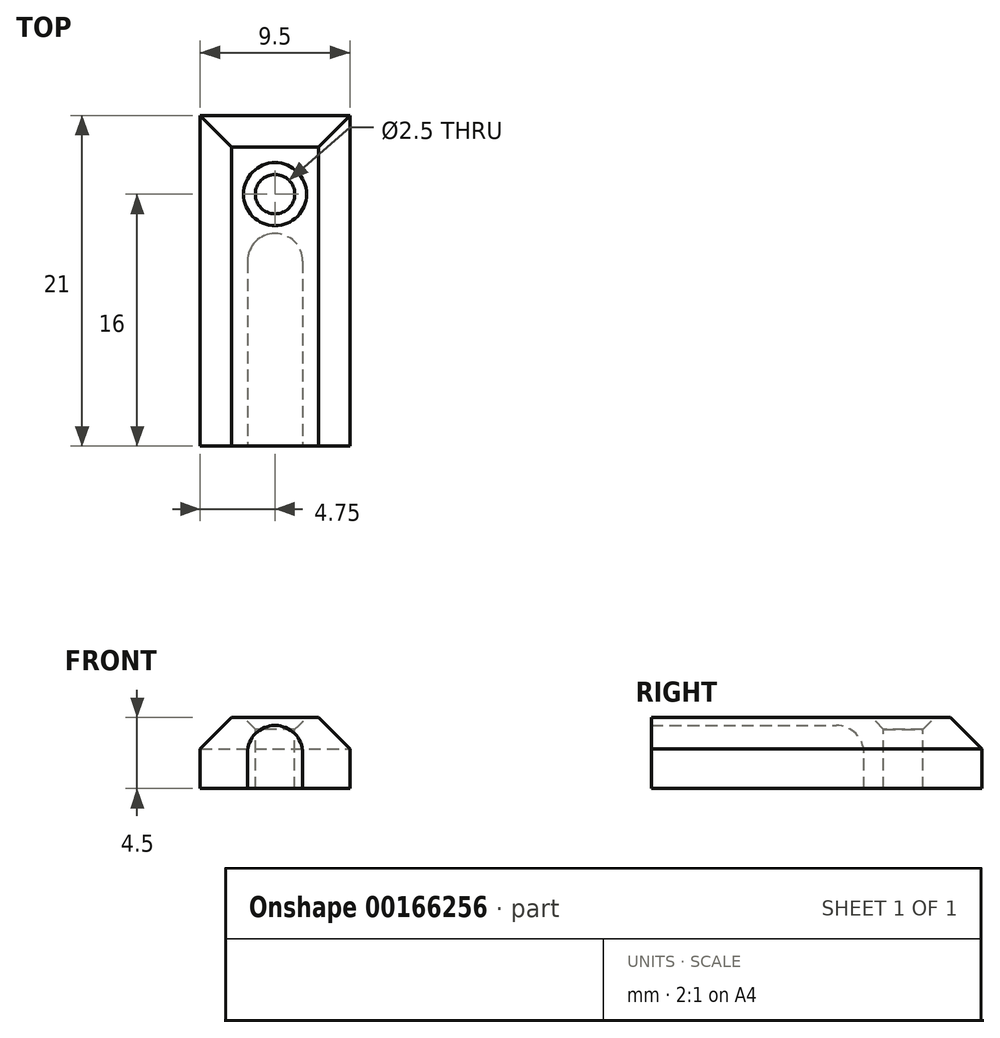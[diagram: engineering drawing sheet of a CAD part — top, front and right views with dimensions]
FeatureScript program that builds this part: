
annotation { "Feature Type Name" : "Feature", "Feature Type Description" : "" }
export const myFeature = defineFeature(function(context is Context, id is Id, definition is map)
    precondition{}
    {
        {
            assignVariable(context, id + "F0", {"name" : "Main_Length", "anyValue" : 21});
        }
        {
            assignVariable(context, id + "F1", {"name" : "Bore_Diam", "anyValue" : 3.5});
        }
        {
            assignVariable(context, id + "F2", {"name" : "Bore_Offset", "anyValue" : 0.5});
        }
        {
            assignVariable(context, id + "F3", {"name" : "Chamfer", "anyValue" : 2});
        }
        {
            assignVariable(context, id + "F4", {"name" : "Hole_Diam", "anyValue" : 2.5});
        }
        {
            var Q0;
            Q0=qCreatedBy(makeId("Front.planeOp"),FACE);
            var sketch = newSketch(context, id + "F5", { "sketchPlane" : qUnion([Q0])});
            skLineSegment(sketch, "E0.bottom", {"start": v(4.75, 4.5) * mm, "end": v(-4.75, 4.5) * mm});
            skLineSegment(sketch, "E0.left", {"start": v(4.75, 4.5) * mm, "end": v(4.75, 0) * mm});
            skLineSegment(sketch, "E0.right", {"start": v(-4.75, 4.5) * mm, "end": v(-4.75, 0) * mm});
            skPoint(sketch, "E0.middle", {"position": v(0, 2.25) * mm});
            skArc(sketch, "E1", {"start": v(1.75, 2.25) * mm, "mid": v(0, 4) * mm, "end": v(-1.75, 2.25) * mm});
            skLineSegment(sketch, "E2", {"start": v(-1.75, 2.25) * mm, "end": v(-1.75, 0) * mm});
            skLineSegment(sketch, "E3", {"start": v(1.75, 2.25) * mm, "end": v(1.75, 0) * mm});
            skLineSegment(sketch, "E4", {"start": v(-4.75, 0) * mm, "end": v(4.75, 0) * mm});
            skSolve(sketch);
        }
        {
            var Q0;
            {var subQ0=sQuery(id+"F5.wireOp",EDGE,"E1");var subQ1=sQuery(id+"F5.wireOp",EDGE,"qxmTr6BR-dzyj-zosj-kyel-UmVIBj9BL0gq");var subQ2=makeQuery(id+"F5.imprint","INTERSECT",VERTEX,{"disambiguationData":[OD(0.0)],"derivedFrom":[subQ1,subQ0]});Q0=makeQuery(id+"F5.imprint","IMPRINT",FACE,{"disambiguationData":[TD([[makeQuery(id+"F5.imprint","IMPRINT",EDGE,{"disambiguationData":[TD([[subQ2,-1.0]])],"derivedFrom":subQ1}),-1.0]])]});}
            var Q1;
            Q1=makeQuery(id+"F5.imprint","IMPRINT",FACE,{"disambiguationData":[TD([[makeQuery(id+"F5.imprint","IMPRINT",EDGE,{"derivedFrom":sQuery(id+"F5.wireOp",EDGE,"E0.bottom")}),1.0]])]});
            var Q2;
            Q2=makeQuery(id+"F5.imprint","IMPRINT",FACE,{"disambiguationData":[TD([[makeQuery(id+"F5.imprint","IMPRINT",EDGE,{"derivedFrom":sQuery(id+"F5.wireOp",EDGE,"E1")}),1.0]])]});
            extrude(context, id + "F6", {"entities" : qUnion([Q0, Q1, Q2]), "oppositeDirection" : true, "depth" : (getVariable(context, 'Main_Length')) * mm});
        }
        {
            var Q0;
            Q0=makeQuery(id+"F6.opExtrude","SWEPT_EDGE",EDGE,{"disambiguationData":[OSD([sQuery(id+"F5.wireOp",EDGE,"E0.bottom"),sQuery(id+"F5.wireOp",EDGE,"E0.right")])]});
            var Q1;
            Q1=makeQuery(id+"F6.opExtrude","SWEPT_EDGE",EDGE,{"disambiguationData":[OSD([sQuery(id+"F5.wireOp",EDGE,"E0.bottom"),sQuery(id+"F5.wireOp",EDGE,"E0.left")])]});
            chamfer(context, id + "F7", {"entities" : qUnion([Q0, Q1]), "width" : (getVariable(context, 'Chamfer')) * mm, "tangentPropagation" : true});
        }
        {
            var Q0;
            Q0=makeQuery(id+"F6.opExtrude","CAP_EDGE",EDGE,{"disambiguationData":[OSD([sQuery(id+"F5.wireOp",EDGE,"E0.bottom")])],"isStart":false});
            chamfer(context, id + "F8", {"entities" : qUnion([Q0]), "width" : (getVariable(context, 'Chamfer')) * mm, "tangentPropagation" : true});
        }
        {
            var Q0;
            Q0=makeQuery(id+"F6.opExtrude","SWEPT_FACE",FACE,{"disambiguationData":[OSD([sQuery(id+"F5.wireOp",EDGE,"E0.bottom")])]});
            cPlane(context, id + "F9", {"entities" : qUnion([Q0]), "cplaneType" : CPlaneType.OFFSET, "offset" : (getVariable(context, 'Bore_Offset') + getVariable(context, 'Bore_Diam') / 2) * mm, "oppositeDirection" : true, "width" : 150 * mm, "height" : 150 * mm});
        }
        {
            var Q0;
            Q0=qCreatedBy(id+"F9.planeOp",FACE);
            var sketch = newSketch(context, id + "F10", { "sketchPlane" : qUnion([Q0])});
            skLineSegment(sketch, "E5", {"start": v(-1.75, 0) * mm, "end": v(-1.75, 11.75) * mm});
            skLineSegment(sketch, "E6", {"start": v(1.75, 0) * mm, "end": v(1.75, 11.75) * mm});
            skArc(sketch, "E7", {"start": v(1.75, 11.75) * mm, "mid": v(0, 13.5) * mm, "end": v(-1.75, 11.75) * mm});
            skLineSegment(sketch, "E8", {"start": v(-1.75, 0) * mm, "end": v(1.75, 0) * mm});
            skLineSegment(sketch, "E9", {"start": v(0, 0) * mm, "end": v(0, 13.5) * mm});
            skSolve(sketch);
        }
        {
            var Q0;
            {var subQ0=sQuery(id+"F10.wireOp",EDGE,"E5");Q0=makeQuery(id+"F10.imprint","IMPRINT",FACE,{"disambiguationData":[TD([[makeQuery(id+"F10.imprint","IMPRINT",EDGE,{"derivedFrom":subQ0}),-1.0]])]});}
            var Q1;
            Q1=sQuery(id+"F10.wireOp",EDGE,"E9");
            revolve(context, id + "F11", {"operationType" : NewBodyOperationType.REMOVE, "entities" : qUnion([Q0]), "axis" : qUnion([Q1]), "revolveType" : RevolveType.FULL, "oppositeDirection" : true});
        }
        {
            var Q0;
            {var subQ0=sQuery(id+"F10.wireOp",EDGE,"E5");Q0=makeQuery(id+"F10.imprint","IMPRINT",FACE,{"disambiguationData":[TD([[makeQuery(id+"F10.imprint","IMPRINT",EDGE,{"derivedFrom":subQ0}),-1.0]])]});}
            var Q1;
            {var subQ0=sQuery(id+"F10.wireOp",EDGE,"E6");Q1=makeQuery(id+"F10.imprint","IMPRINT",FACE,{"disambiguationData":[TD([[makeQuery(id+"F10.imprint","IMPRINT",EDGE,{"derivedFrom":subQ0}),1.0]])]});}
            extrude(context, id + "F12", {"entities" : qUnion([Q0, Q1]), "operationType" : NewBodyOperationType.REMOVE, "endBound" : BoundingType.THROUGH_ALL, "oppositeDirection" : true, "depth" : 25 * mm});
        }
        {
            var Q0;
            Q0=makeQuery(id+"F6.opExtrude","SWEPT_FACE",FACE,{"disambiguationData":[OSD([sQuery(id+"F5.wireOp",EDGE,"E0.bottom")])]});
            var sketch = newSketch(context, id + "F13", { "sketchPlane" : qUnion([Q0])});
            skCircle(sketch, "E10", {"center": v(0, 16) * mm, "radius": 1.25 * mm});
            skSolve(sketch);
        }
        {
            var Q0;
            Q0=sQuery(id+"F13.wireOp",VERTEX,"E10.center");
            var Q1;
            Q1=makeQuery(id+"F6.opExtrude","SWEPT_BODY",BODY,{"disambiguationData":[OSD([sQuery(id+"F5.wireOp",EDGE,"qxmTr6BR-dzyj-zosj-kyel-UmVIBj9BL0gq"),sQuery(id+"F5.wireOp",EDGE,"E0.bottom"),sQuery(id+"F5.wireOp",EDGE,"E0.left"),sQuery(id+"F5.wireOp",EDGE,"E0.right")])]});
            hole(context, id + "F14", {"style" : HoleStyle.C_SINK, "endStyle" : HoleEndStyle.THROUGH, "holeDiameter" : (getVariable(context, 'Hole_Diam')) * mm, "cSinkDiameter" : 4 * mm, "cSinkAngle" : 90 * degree, "locations" : qUnion([Q0]), "scope" : qUnion([Q1]), "isTappedThrough" : true});
        }
    });
